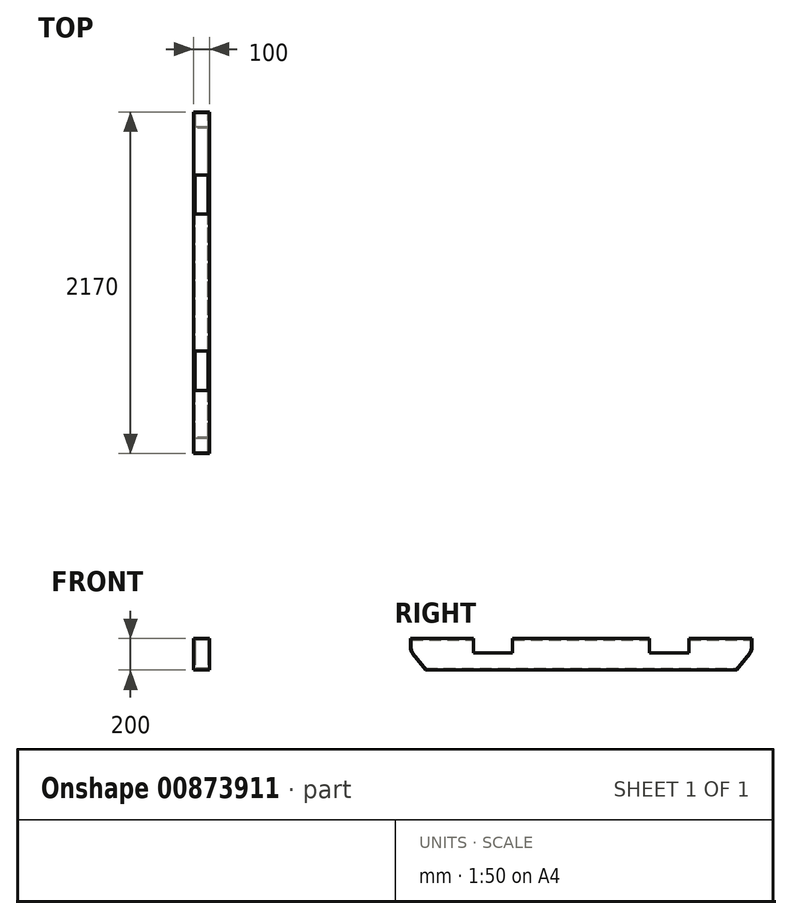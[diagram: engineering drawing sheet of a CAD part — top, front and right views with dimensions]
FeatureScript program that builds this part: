
annotation { "Feature Type Name" : "Feature", "Feature Type Description" : "" }
export const myFeature = defineFeature(function(context is Context, id is Id, definition is map)
    precondition{}
    {
        {
            var Q0;
            Q0=qCreatedBy(makeId("Front.planeOp"),FACE);
            var sketch = newSketch(context, id + "F0", { "sketchPlane" : qUnion([Q0])});
            skLineSegment(sketch, "E0.bottom", {"start": v(50, 100) * mm, "end": v(-50, 100) * mm});
            skLineSegment(sketch, "E0.top", {"start": v(50, -100) * mm, "end": v(-50, -100) * mm});
            skLineSegment(sketch, "E0.right", {"start": v(-50, 100) * mm, "end": v(-50, -100) * mm});
            skPoint(sketch, "E0.middle", {"position": v(0, 0) * mm});
            skLineSegment(sketch, "E1.0", {"start": v(41, -91) * mm, "end": v(-41, -91) * mm});
            skLineSegment(sketch, "E1.1", {"start": v(-41, 91) * mm, "end": v(-41, -91) * mm});
            skLineSegment(sketch, "E1.2", {"start": v(41, 91) * mm, "end": v(-41, 91) * mm});
            skLineSegment(sketch, "E2", {"start": v(50, 100) * mm, "end": v(50, -100) * mm});
            skLineSegment(sketch, "E3.0", {"start": v(41, 91) * mm, "end": v(41, -91) * mm});
            skSolve(sketch);
        }
        {
            var Q0;
            Q0=makeQuery(id+"F0.imprint","IMPRINT",FACE,{"disambiguationData":[TD([[makeQuery(id+"F0.imprint","IMPRINT",EDGE,{"derivedFrom":sQuery(id+"F0.wireOp",EDGE,"E0.bottom")}),1.0]])]});
            extrude(context, id + "F1", {"entities" : qUnion([Q0]), "depth" : 2160 * mm, "offsetDistance" : 25 * mm, "symmetric" : true});
        }
        {
            var Q0;
            Q0=makeQuery(id+"F1.opExtrude","SWEPT_FACE",FACE,{"disambiguationData":[OSD([sQuery(id+"F0.wireOp",EDGE,"E0.right")])]});
            var sketch = newSketch(context, id + "F2", { "sketchPlane" : qUnion([Q0])});
            skLineSegment(sketch, "E4", {"start": v(-1080, -100) * mm, "end": v(-1080, 43) * mm, "construction": true});
            skLineSegment(sketch, "E5", {"start": v(-1080, -100) * mm, "end": v(-981.5, -100) * mm, "construction": true});
            skLineSegment(sketch, "E6", {"start": v(-981.5, -100) * mm, "end": v(-981.5, -209) * mm});
            skLineSegment(sketch, "E7", {"start": v(-981.5, -209) * mm, "end": v(-1186.23, -209) * mm});
            skLineSegment(sketch, "E8", {"start": v(-1186.23, -209) * mm, "end": v(-1186.23, 43) * mm});
            skLineSegment(sketch, "E9", {"start": v(-1186.23, 43) * mm, "end": v(-1080, 43) * mm});
            skLineSegment(sketch, "E10", {"start": v(-1080, 100) * mm, "end": v(-685, 100) * mm, "construction": true});
            skLineSegment(sketch, "E11", {"start": v(-685, 100) * mm, "end": v(-685, 10) * mm, "construction": true});
            skLineSegment(sketch, "E12.bottom", {"start": v(-685, 10) * mm, "end": v(-435, 10) * mm});
            skLineSegment(sketch, "E12.top", {"start": v(-685, 233.7) * mm, "end": v(-435, 233.7) * mm});
            skLineSegment(sketch, "E12.left", {"start": v(-685, 10) * mm, "end": v(-685, 233.7) * mm});
            skLineSegment(sketch, "E12.right", {"start": v(-435, 10) * mm, "end": v(-435, 233.7) * mm});
            skLineSegment(sketch, "E13.MirrorCS", {"start": v(981.5, -209) * mm, "end": v(1186.23, -209) * mm});
            skLineSegment(sketch, "E14.MirrorCS", {"start": v(1186.23, -209) * mm, "end": v(1186.23, 43) * mm});
            skLineSegment(sketch, "E15.MirrorCS", {"start": v(1080, -100) * mm, "end": v(981.5, -100) * mm, "construction": true});
            skLineSegment(sketch, "E16.MirrorCS", {"start": v(981.5, -100) * mm, "end": v(981.5, -209) * mm});
            skLineSegment(sketch, "E17.MirrorCS", {"start": v(1186.23, 43) * mm, "end": v(1080, 43) * mm});
            skLineSegment(sketch, "E18.MirrorCS", {"start": v(1080, -100) * mm, "end": v(1080, 43) * mm, "construction": true});
            skLineSegment(sketch, "E19.MirrorCS", {"start": v(435, 10) * mm, "end": v(435, 233.7) * mm});
            skLineSegment(sketch, "E20.MirrorCS", {"start": v(685, 10) * mm, "end": v(685, 233.7) * mm});
            skLineSegment(sketch, "E21.MirrorCS", {"start": v(685, 233.7) * mm, "end": v(435, 233.7) * mm});
            skLineSegment(sketch, "E22.MirrorCS", {"start": v(685, 100) * mm, "end": v(685, 10) * mm, "construction": true});
            skLineSegment(sketch, "E23.MirrorCS", {"start": v(685, 10) * mm, "end": v(435, 10) * mm});
            skLineSegment(sketch, "E24.bottom", {"start": v(-1080, 100) * mm, "end": v(-1022.85, 100) * mm, "construction": true});
            skLineSegment(sketch, "E24.top", {"start": v(-1080, 42.85) * mm, "end": v(-1022.85, 42.85) * mm, "construction": true});
            skLineSegment(sketch, "E24.left", {"start": v(-1080, 100) * mm, "end": v(-1080, 42.85) * mm, "construction": true});
            skLineSegment(sketch, "E24.right", {"start": v(-1022.85, 100) * mm, "end": v(-1022.85, 42.85) * mm, "construction": true});
            skArc(sketch, "E25", {"start": v(-1080, 43) * mm, "mid": v(-1076.79, 23.96) * mm, "end": v(-1067.42, 7.08) * mm});
            skLineSegment(sketch, "E26", {"start": v(-981.5, -100) * mm, "end": v(-1067.42, 7.08) * mm});
            skArc(sketch, "E27.trimOffspring", {"start": v(-1022.7, 100) * mm, "mid": v(-1022.85, 100) * mm, "end": v(-1023, 100) * mm});
            skLineSegment(sketch, "E28.MirrorCS", {"start": v(981.5, -100) * mm, "end": v(1067.42, 7.08) * mm});
            skArc(sketch, "E29.MirrorCS", {"start": v(1080, 43) * mm, "mid": v(1076.79, 23.96) * mm, "end": v(1067.42, 7.08) * mm});
            skSolve(sketch);
        }
        {
            var Q0;
            Q0 = qSketchRegion(id + "F2", true);
            extrude(context, id + "F3", {"entities" : qUnion([Q0]), "operationType" : NewBodyOperationType.REMOVE, "endBound" : BoundingType.THROUGH_ALL, "oppositeDirection" : true, "depth" : 25 * mm, "offsetDistance" : 25 * mm});
        }
        {
            var Q0;
            Q0=makeQuery(id+"F1.opExtrude","SWEPT_FACE",FACE,{"disambiguationData":[OSD([sQuery(id+"F0.wireOp",EDGE,"E0.right")])]});
            var sketch = newSketch(context, id + "F4", { "sketchPlane" : qUnion([Q0])});
            skLineSegment(sketch, "E30", {"start": v(-981.5, -100) * mm, "end": v(-1067.42, 7.08) * mm});
            skLineSegment(sketch, "E31", {"start": v(-1080, 100) * mm, "end": v(-1080, 42.7) * mm});
            skArc(sketch, "E32", {"start": v(-1080, 42.7) * mm, "mid": v(-1076.74, 23.82) * mm, "end": v(-1067.42, 7.08) * mm});
            skLineSegment(sketch, "E33.0", {"start": v(-1085, 100) * mm, "end": v(-1085, 42.7) * mm});
            skArc(sketch, "E33.1", {"start": v(-1085, 42.7) * mm, "mid": v(-1081.46, 22.16) * mm, "end": v(-1071.32, 3.95) * mm});
            skLineSegment(sketch, "E33.2", {"start": v(-987.91, -100) * mm, "end": v(-1071.32, 3.95) * mm});
            skLineSegment(sketch, "E34", {"start": v(-1085, 100) * mm, "end": v(-1080, 100) * mm});
            skLineSegment(sketch, "E35", {"start": v(-981.5, -100) * mm, "end": v(-987.91, -100) * mm});
            skLineSegment(sketch, "E36.MirrorCS", {"start": v(1085, 100) * mm, "end": v(1080, 100) * mm});
            skArc(sketch, "E37.MirrorCS", {"start": v(1085, 42.7) * mm, "mid": v(1081.46, 22.16) * mm, "end": v(1071.32, 3.95) * mm});
            skArc(sketch, "E38.MirrorCS", {"start": v(1080, 42.7) * mm, "mid": v(1076.74, 23.82) * mm, "end": v(1067.42, 7.08) * mm});
            skLineSegment(sketch, "E39.MirrorCS", {"start": v(981.5, -100) * mm, "end": v(987.91, -100) * mm});
            skLineSegment(sketch, "E40.MirrorCS", {"start": v(1080, 100) * mm, "end": v(1080, 42.7) * mm});
            skLineSegment(sketch, "E41.MirrorCS", {"start": v(981.5, -100) * mm, "end": v(1067.42, 7.08) * mm});
            skLineSegment(sketch, "E42.MirrorCS", {"start": v(987.91, -100) * mm, "end": v(1071.32, 3.95) * mm});
            skLineSegment(sketch, "E43.MirrorCS", {"start": v(1085, 100) * mm, "end": v(1085, 42.7) * mm});
            skSolve(sketch);
        }
        {
            var Q0;
            Q0 = qSketchRegion(id + "F4", true);
            extrude(context, id + "F5", {"entities" : qUnion([Q0]), "operationType" : NewBodyOperationType.REMOVE, "endBound" : BoundingType.THROUGH_ALL, "oppositeDirection" : true, "depth" : 25 * mm, "offsetDistance" : 25 * mm});
        }
        {
            var Q0;
            Q0 = qSketchRegion(id + "F4", true);
            var Q1;
            Q1=makeQuery(id+"F1.opExtrude","SWEPT_FACE",FACE,{"disambiguationData":[OSD([sQuery(id+"F0.wireOp",EDGE,"E2")])]});
            extrude(context, id + "F6", {"entities" : qUnion([Q0]), "endBound" : BoundingType.UP_TO_SURFACE, "oppositeDirection" : true, "depth" : 25 * mm, "endBoundEntityFace" : qUnion([Q1]), "offsetDistance" : 25 * mm});
        }
    });
